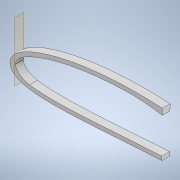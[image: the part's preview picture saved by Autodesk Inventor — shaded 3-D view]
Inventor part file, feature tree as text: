
AUTODESK INVENTOR PART (.ipt)
format: ipt  version: 2022.3 (Build 263350000, 350)  size: 483,840 bytes
history: native  units: mm
features: sketch x5, extrude x4, thicken_offset x3, projected_geometry x2, shell x1, plane x1, other x1
ambient origin geometry x8: Origin, YZ Plane, XZ Plane, XY Plane, X Axis, Y Axis, Z Axis, Center Point
bodies: Solid1 (feature_tree)
feature tree (17):
  extrude  "Extrusion1"  Depth=10.0mm
  shell  "Shell1"  Thickness=1.0mm
  thicken_offset  "Thicken1"
  extrude  "Extrusion27"  TaperAngle=0.0deg  [1 undecoded]
  thicken_offset  "Thicken3"
  extrude  "Extrusion29"  Depth=20.0mm
  plane  "Work Plane5"
  other  "Bend Part2"
  thicken_offset  "Thicken5"
  extrude  "Extrusion30"  Depth=10.0mm TaperAngle=0.0deg
  sketch  "Sketch3"  dims[d0=10.0mm d1=0.0mm d2=3.0mm d159=1.0mm d160=2.0mm]
  sketch  "Sketch48"  dims[d236=190.0mm d237=0.0mm d238=0.0mm]
  sketch  "Sketch55"  dims[d249=2.0mm d250=1.0mm d254=20.0mm]
  projected_geometry  "Projected Loop32"
  sketch  "Sketch57"  dims[d255=8.0mm d256=10.0mm d257=0.0mm]
  sketch  "Sketch58"  dims[d262=10.0mm d263=0.349066mm d264=1.0mm d265=1.0mm d268=50.0mm d269=3.0mm d270=10.0mm d271=0.0mm]
  projected_geometry  "Projected Loop34"
note: 1 required parameter value undecoded (feature->parameter linkage not recoverable at this tier; creation-order binding heuristic only, values carry confidence <= 0.55)
